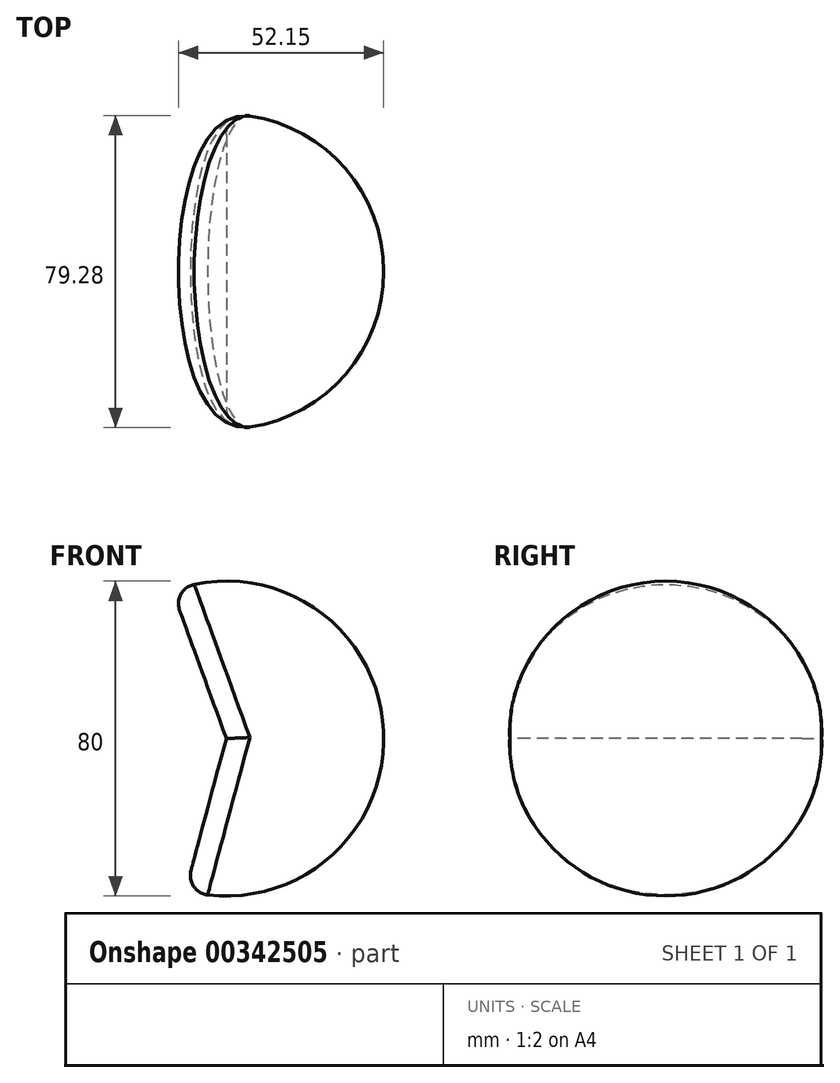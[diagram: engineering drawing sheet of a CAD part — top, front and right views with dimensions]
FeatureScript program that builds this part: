
annotation { "Feature Type Name" : "Feature", "Feature Type Description" : "" }
export const myFeature = defineFeature(function(context is Context, id is Id, definition is map)
    precondition{}
    {
        {
            var Q0;
            Q0=qCreatedBy(makeId("Top.planeOp"),FACE);
            var sketch = newSketch(context, id + "F0", { "sketchPlane" : qUnion([Q0])});
            skCircle(sketch, "E0", {"center": v(0, 0) * mm, "radius": 40 * mm});
            skLineSegment(sketch, "E1", {"start": v(0, 40) * mm, "end": v(0, -40) * mm});
            skSolve(sketch);
        }
        {
            var Q0;
            {var subQ0=sQuery(id+"F0.wireOp",EDGE,"E1");Q0=makeQuery(id+"F0.imprint","IMPRINT",FACE,{"disambiguationData":[TD([[makeQuery(id+"F0.imprint","IMPRINT",EDGE,{"derivedFrom":subQ0}),1.0]])]});}
            var Q1;
            Q1=sQuery(id+"F0.wireOp",EDGE,"E1");
            revolve(context, id + "F1", {"entities" : qUnion([Q0]), "axis" : qUnion([Q1]), "revolveType" : RevolveType.TWO_DIRECTIONS, "angle" : 110 * degree, "angleBack" : 255 * degree});
        }
        {
            var Q0;
            Q0=makeQuery(id+"F1.opRevolve","CAP_EDGE",EDGE,{"disambiguationData":[OSD([sQuery(id+"F0.wireOp",EDGE,"E0")])],"isStart":false});
            var Q1;
            Q1=makeQuery(id+"F1.opRevolve","CAP_EDGE",EDGE,{"disambiguationData":[OSD([sQuery(id+"F0.wireOp",EDGE,"E0")])],"isStart":true});
            fillet(context, id + "F2", {"entities" : qUnion([Q0, Q1]), "radius" : 5 * mm, "tangentPropagation" : true, "allowEdgeOverflow" : false});
        }
    });
